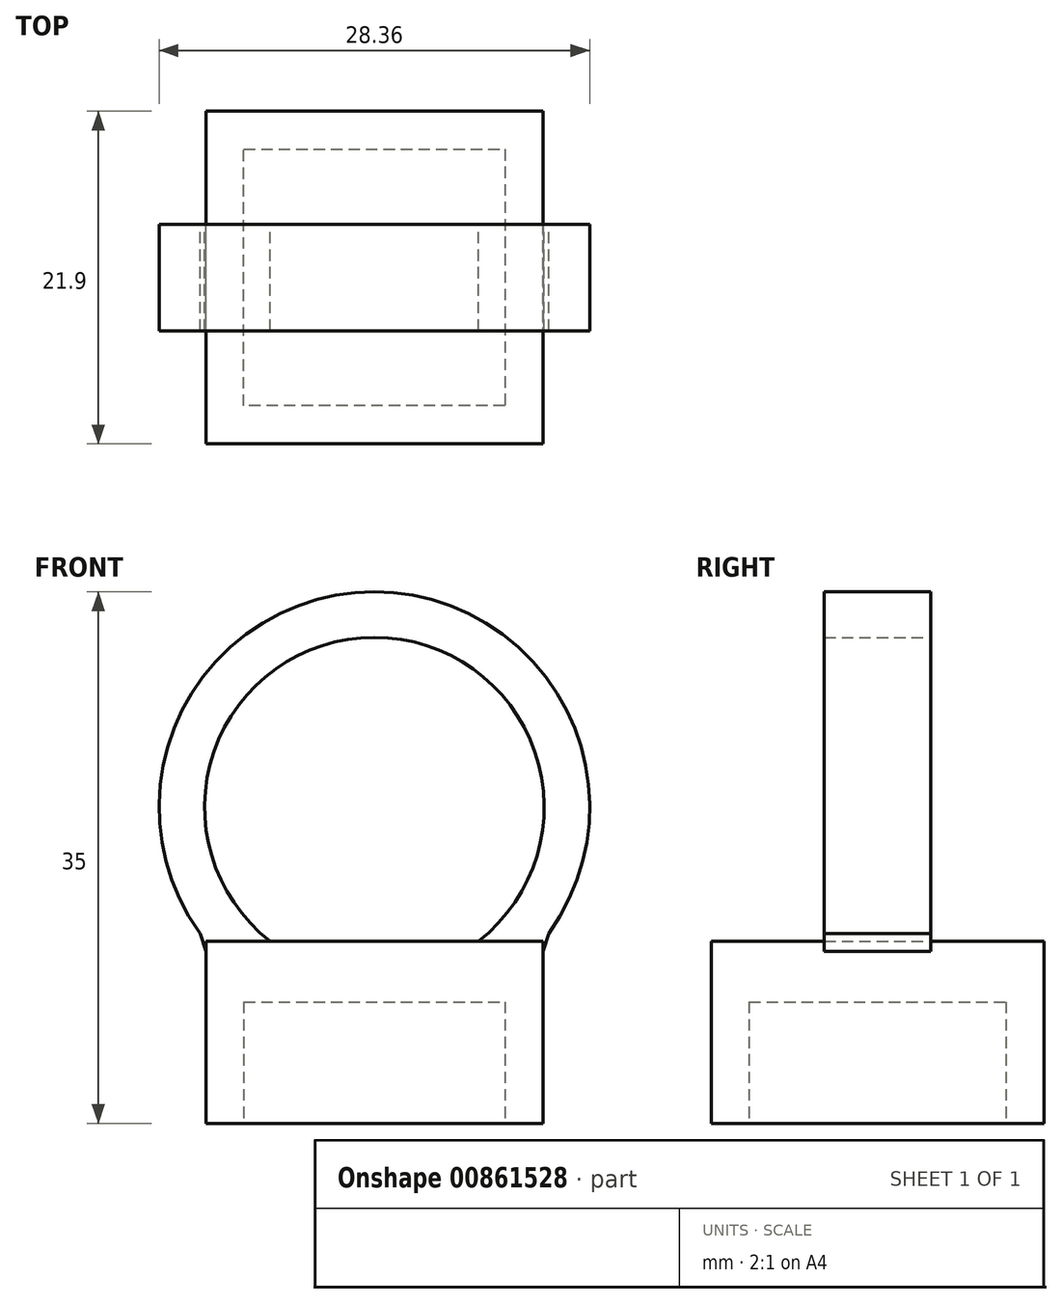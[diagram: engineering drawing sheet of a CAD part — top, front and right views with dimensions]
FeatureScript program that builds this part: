
annotation { "Feature Type Name" : "Feature", "Feature Type Description" : "" }
export const myFeature = defineFeature(function(context is Context, id is Id, definition is map)
    precondition{}
    {
        {
            var Q0;
            Q0=qCreatedBy(makeId("Front.planeOp"),FACE);
            var sketch = newSketch(context, id + "F0", { "sketchPlane" : qUnion([Q0])});
            skLineSegment(sketch, "E0.bottom", {"start": v(11.1, 6) * mm, "end": v(-11.1, 6) * mm});
            skLineSegment(sketch, "E0.top", {"start": v(11.1, -6) * mm, "end": v(-11.1, -6) * mm});
            skLineSegment(sketch, "E0.left", {"start": v(11.1, 6) * mm, "end": v(11.1, -6) * mm});
            skLineSegment(sketch, "E0.right", {"start": v(-11.1, 6) * mm, "end": v(-11.1, -6) * mm});
            skPoint(sketch, "E0.middle", {"position": v(0, 0) * mm});
            skArc(sketch, "E1", {"start": v(11.1, 6) * mm, "mid": v(0, 29) * mm, "end": v(-11.1, 6) * mm});
            skArc(sketch, "E2.0", {"start": v(6.87, 6) * mm, "mid": v(0, 26) * mm, "end": v(-6.87, 6) * mm});
            skSolve(sketch);
        }
        {
            var Q0;
            Q0=makeQuery(id+"F0.imprint","IMPRINT",FACE,{"disambiguationData":[TD([[makeQuery(id+"F0.imprint","IMPRINT",EDGE,{"derivedFrom":sQuery(id+"F0.wireOp",EDGE,"E0.top")}),-1.0]])]});
            extrude(context, id + "F1", {"entities" : qUnion([Q0]), "endBound" : BoundingType.SYMMETRIC, "depth" : 21.9 * mm, "offsetDistance" : 25 * mm});
        }
        {
            var Q0;
            {var subQ0=sQuery(id+"F0.wireOp",EDGE,"E1");Q0=makeQuery(id+"F0.imprint","IMPRINT",FACE,{"disambiguationData":[TD([[makeQuery(id+"F0.imprint","IMPRINT",EDGE,{"derivedFrom":subQ0}),1.0]])]});}
            extrude(context, id + "F2", {"entities" : qUnion([Q0]), "operationType" : NewBodyOperationType.ADD, "endBound" : BoundingType.SYMMETRIC, "depth" : 7 * mm, "offsetDistance" : 25 * mm});
        }
        {
            var Q0;
            Q0=qCreatedBy(makeId("Top.planeOp"),FACE);
            cPlane(context, id + "F3", {"entities" : qUnion([Q0]), "cplaneType" : CPlaneType.OFFSET, "offset" : 6 * mm, "oppositeDirection" : true, "width" : 150 * mm, "height" : 150 * mm});
        }
        {
            var Q0;
            Q0=qCreatedBy(id+"F3.planeOp",FACE);
            var sketch = newSketch(context, id + "F4", { "sketchPlane" : qUnion([Q0])});
            skLineSegment(sketch, "E3.0", {"start": v(-8.6, 8.45) * mm, "end": v(8.6, 8.45) * mm});
            skLineSegment(sketch, "E3.1", {"start": v(-8.6, -8.45) * mm, "end": v(-8.6, 8.45) * mm});
            skLineSegment(sketch, "E3.2", {"start": v(8.6, -8.45) * mm, "end": v(-8.6, -8.45) * mm});
            skLineSegment(sketch, "E3.3", {"start": v(8.6, 8.45) * mm, "end": v(8.6, -8.45) * mm});
            skSolve(sketch);
        }
        {
            var Q0;
            Q0=makeQuery(id+"F4.imprint","IMPRINT",FACE,{"disambiguationData":[TD([[makeQuery(id+"F4.imprint","IMPRINT",EDGE,{"derivedFrom":sQuery(id+"F4.wireOp",EDGE,"E3.0")}),-1.0]])]});
            extrude(context, id + "F5", {"entities" : qUnion([Q0]), "operationType" : NewBodyOperationType.REMOVE, "depth" : 8 * mm, "offsetDistance" : 25 * mm});
        }
        {
            var Q0;
            {var subQ0=sQuery(id+"F0.wireOp",EDGE,"E1");var subQ1=sQuery(id+"F0.wireOp",EDGE,"E0.left");var subQ2=sQuery(id+"F0.wireOp",EDGE,"E0.bottom");Q0=makeQuery(id+"F2.boolean.opBoolean","MERGE",EDGE,{"derivedFrom":[makeQuery(id+"F1.opExtrude","SWEPT_EDGE",EDGE,{"disambiguationData":[OSD([subQ2,subQ1,subQ0])]}),makeQuery(id+"F2.opExtrude","SWEPT_EDGE",EDGE,{"disambiguationData":[OSD([subQ2,subQ1,subQ0])]})]});}
            var Q1;
            {var subQ0=sQuery(id+"F0.wireOp",EDGE,"E1");var subQ1=sQuery(id+"F0.wireOp",EDGE,"E0.right");var subQ2=sQuery(id+"F0.wireOp",EDGE,"E0.bottom");Q1=makeQuery(id+"F2.boolean.opBoolean","MERGE",EDGE,{"derivedFrom":[makeQuery(id+"F1.opExtrude","SWEPT_EDGE",EDGE,{"disambiguationData":[OSD([subQ2,subQ1,subQ0])]}),makeQuery(id+"F2.opExtrude","SWEPT_EDGE",EDGE,{"disambiguationData":[OSD([subQ2,subQ1,subQ0])]})]});}
            var Q2;
            {var subQ0=sQuery(id+"F0.wireOp",EDGE,"E0.bottom");Q2=makeQuery(id+"F2.opExtrude","CAP_EDGE",EDGE,{"disambiguationData":[OSD([subQ0]),TDD([makeQuery(id+"F0.imprint","IMPRINT",EDGE,{"disambiguationData":[TD([[makeQuery(id+"F0.imprint","INTERSECT",VERTEX,{"disambiguationData":[OD(1.0)],"derivedFrom":[subQ0,sQuery(id+"F0.wireOp",EDGE,"E2.0")]}),-1.0]])],"derivedFrom":subQ0})])],"isStart":true});}
            var Q3;
            {var subQ0=sQuery(id+"F0.wireOp",EDGE,"E0.bottom");Q3=makeQuery(id+"F2.opExtrude","CAP_EDGE",EDGE,{"disambiguationData":[OSD([subQ0]),TDD([makeQuery(id+"F0.imprint","IMPRINT",EDGE,{"disambiguationData":[TD([[makeQuery(id+"F0.imprint","INTERSECT",VERTEX,{"disambiguationData":[OD(0.0)],"derivedFrom":[subQ0,sQuery(id+"F0.wireOp",EDGE,"E2.0")]}),1.0]])],"derivedFrom":subQ0})])],"isStart":true});}
            var Q4;
            {var subQ0=sQuery(id+"F0.wireOp",EDGE,"E0.bottom");Q4=makeQuery(id+"F2.opExtrude","CAP_EDGE",EDGE,{"disambiguationData":[OSD([subQ0]),TDD([makeQuery(id+"F0.imprint","IMPRINT",EDGE,{"disambiguationData":[TD([[makeQuery(id+"F0.imprint","INTERSECT",VERTEX,{"disambiguationData":[OD(0.0)],"derivedFrom":[subQ0,sQuery(id+"F0.wireOp",EDGE,"E2.0")]}),1.0]])],"derivedFrom":subQ0})])],"isStart":false});}
            var Q5;
            {var subQ0=sQuery(id+"F0.wireOp",EDGE,"E0.bottom");Q5=makeQuery(id+"F2.opExtrude","CAP_EDGE",EDGE,{"disambiguationData":[OSD([subQ0]),TDD([makeQuery(id+"F0.imprint","IMPRINT",EDGE,{"disambiguationData":[TD([[makeQuery(id+"F0.imprint","INTERSECT",VERTEX,{"disambiguationData":[OD(1.0)],"derivedFrom":[subQ0,sQuery(id+"F0.wireOp",EDGE,"E2.0")]}),-1.0]])],"derivedFrom":subQ0})])],"isStart":false});}
            var Q6;
            {var subQ0=sQuery(id+"F0.wireOp",EDGE,"E2.0");var subQ1=sQuery(id+"F0.wireOp",EDGE,"E0.bottom");Q6=makeQuery(id+"F2.opExtrude","SWEPT_EDGE",EDGE,{"disambiguationData":[OSD([subQ1,subQ0]),TDD([makeQuery(id+"F0.imprint","INTERSECT",VERTEX,{"disambiguationData":[OD(0.0)],"derivedFrom":[subQ1,subQ0]})])]});}
            var Q7;
            {var subQ0=sQuery(id+"F0.wireOp",EDGE,"E2.0");var subQ1=sQuery(id+"F0.wireOp",EDGE,"E0.bottom");Q7=makeQuery(id+"F2.opExtrude","SWEPT_EDGE",EDGE,{"disambiguationData":[OSD([subQ1,subQ0]),TDD([makeQuery(id+"F0.imprint","INTERSECT",VERTEX,{"disambiguationData":[OD(1.0)],"derivedFrom":[subQ1,subQ0]})])]});}
            chamfer(context, id + "F6", {"entities" : qUnion([Q0, Q1, Q2, Q3, Q4, Q5, Q6, Q7]), "width" : 2 * mm, "tangentPropagation" : true});
        }
    });
